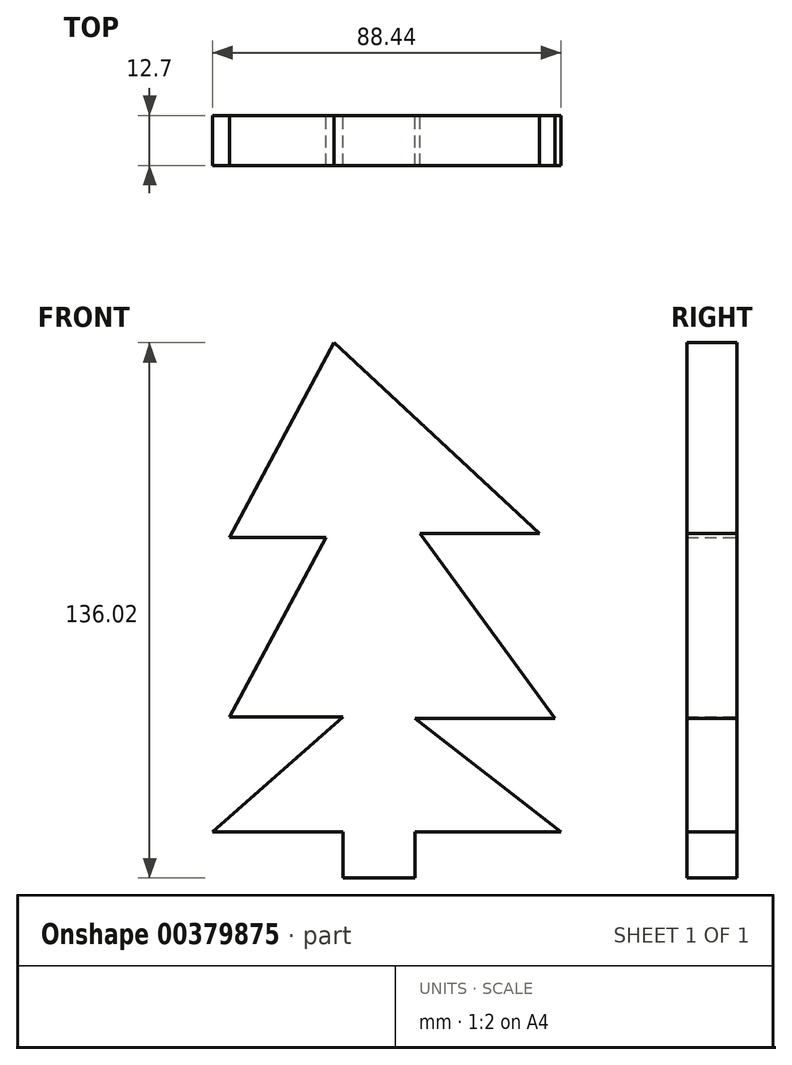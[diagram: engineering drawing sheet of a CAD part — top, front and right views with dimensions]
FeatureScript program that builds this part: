
annotation { "Feature Type Name" : "Feature", "Feature Type Description" : "" }
export const myFeature = defineFeature(function(context is Context, id is Id, definition is map)
    precondition{}
    {
        {
            var Q0;
            Q0=qCreatedBy(makeId("Front.planeOp"),FACE);
            var sketch = newSketch(context, id + "F0", { "sketchPlane" : qUnion([Q0])});
            skLineSegment(sketch, "E0", {"start": v(2.08, 59.55) * mm, "end": v(-24.39, 10.05) * mm});
            skLineSegment(sketch, "E1", {"start": v(-24.39, 10.05) * mm, "end": v(0, 10.05) * mm});
            skLineSegment(sketch, "E2", {"start": v(2.08, 59.55) * mm, "end": v(54.33, 11.11) * mm});
            skLineSegment(sketch, "E3", {"start": v(54.33, 11.11) * mm, "end": v(23.97, 11.11) * mm});
            skLineSegment(sketch, "E4", {"start": v(23.97, 11.11) * mm, "end": v(58.28, -35.94) * mm});
            skLineSegment(sketch, "E5", {"start": v(0, 10.05) * mm, "end": v(-24.39, -35.57) * mm});
            skLineSegment(sketch, "E6", {"start": v(-24.39, -35.57) * mm, "end": v(4.37, -35.57) * mm});
            skLineSegment(sketch, "E7", {"start": v(4.37, -35.57) * mm, "end": v(-28.73, -64.72) * mm});
            skLineSegment(sketch, "E8", {"start": v(-28.73, -64.72) * mm, "end": v(4.37, -64.72) * mm});
            skLineSegment(sketch, "E9", {"start": v(4.37, -64.72) * mm, "end": v(4.37, -76.47) * mm});
            skLineSegment(sketch, "E10", {"start": v(4.37, -76.47) * mm, "end": v(22.68, -76.47) * mm});
            skLineSegment(sketch, "E11", {"start": v(22.68, -76.47) * mm, "end": v(22.68, -64.72) * mm});
            skLineSegment(sketch, "E12", {"start": v(22.68, -64.72) * mm, "end": v(59.7, -64.72) * mm});
            skLineSegment(sketch, "E13", {"start": v(58.28, -35.94) * mm, "end": v(22.68, -35.94) * mm});
            skLineSegment(sketch, "E14", {"start": v(22.68, -35.94) * mm, "end": v(59.7, -64.72) * mm});
            skSolve(sketch);
        }
        {
            var Q0;
            Q0 = qSketchRegion(id + "F0", true);
            extrude(context, id + "F1", {"entities" : qUnion([Q0]), "depth" : 12.7 * mm});
        }
    });
